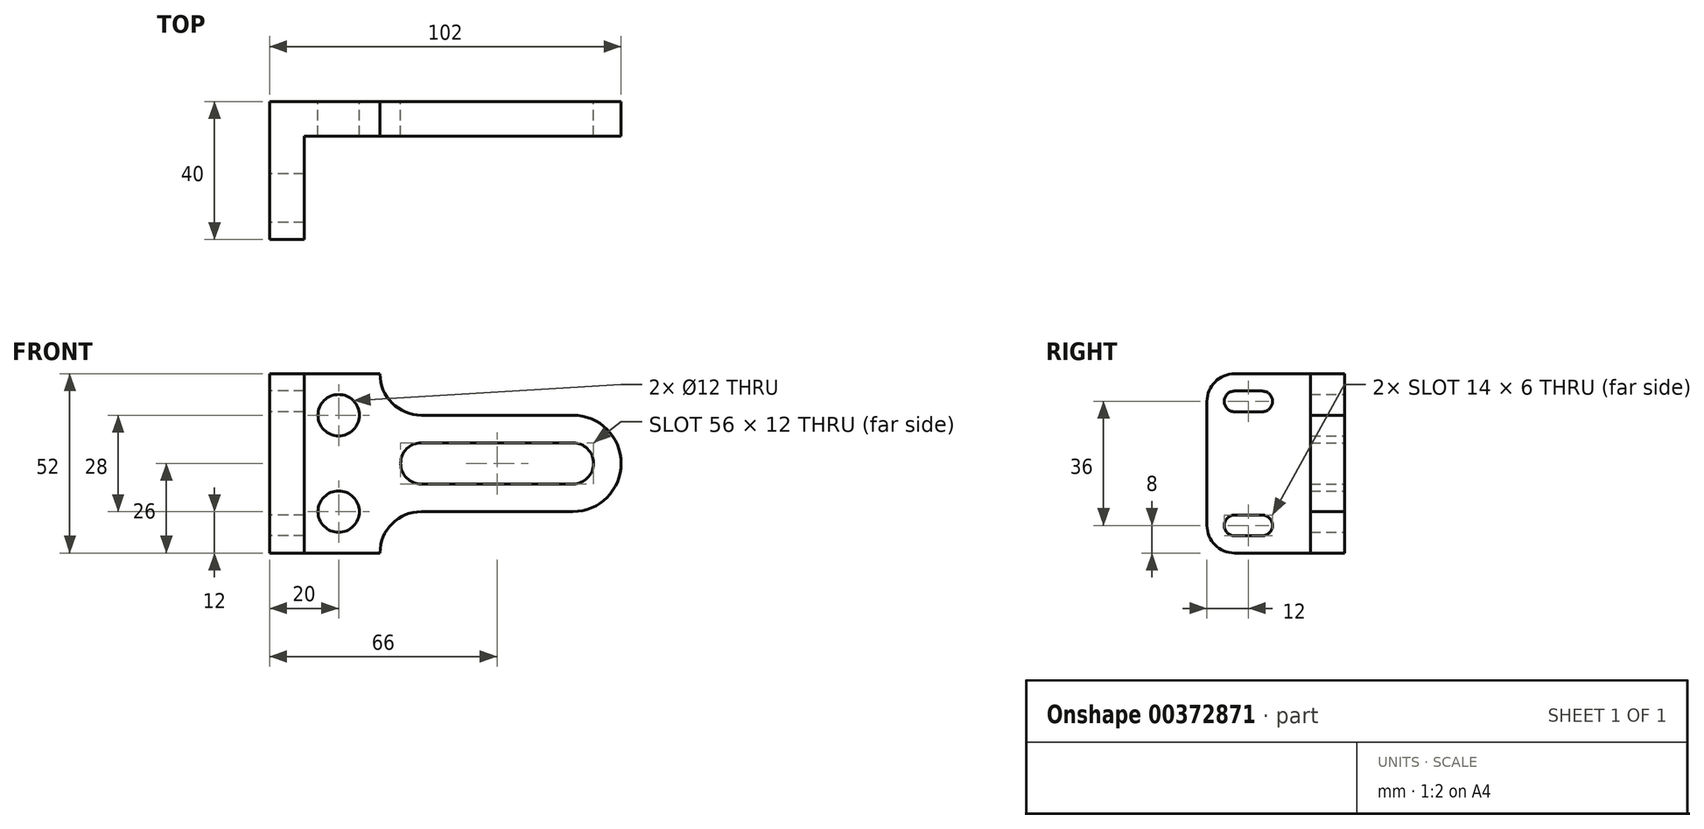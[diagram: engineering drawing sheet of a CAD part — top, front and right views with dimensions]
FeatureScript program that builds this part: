
annotation { "Feature Type Name" : "Feature", "Feature Type Description" : "" }
export const myFeature = defineFeature(function(context is Context, id is Id, definition is map)
    precondition{}
    {
        {
            var Q0;
            Q0=qCreatedBy(makeId("Front.planeOp"),FACE);
            var sketch = newSketch(context, id + "F0", { "sketchPlane" : qUnion([Q0])});
            skLineSegment(sketch, "E0", {"start": v(0, 52) * mm, "end": v(32, 52) * mm});
            skLineSegment(sketch, "E1", {"start": v(32, 52) * mm, "end": v(32, 40) * mm});
            skLineSegment(sketch, "E2", {"start": v(32, 40) * mm, "end": v(88, 40) * mm});
            skLineSegment(sketch, "E3", {"start": v(88, 12) * mm, "end": v(32, 12) * mm});
            skLineSegment(sketch, "E4", {"start": v(32, 12) * mm, "end": v(32, 0) * mm});
            skLineSegment(sketch, "E5", {"start": v(32, 0) * mm, "end": v(0, 0) * mm});
            skLineSegment(sketch, "E6", {"start": v(0, 0) * mm, "end": v(0, 52) * mm});
            skArc(sketch, "E7", {"start": v(88, 12) * mm, "mid": v(102, 26) * mm, "end": v(88, 40) * mm});
            skArc(sketch, "E8", {"start": v(44, 32) * mm, "mid": v(38, 26) * mm, "end": v(44, 20) * mm});
            skArc(sketch, "E9", {"start": v(88, 20) * mm, "mid": v(94, 26) * mm, "end": v(88, 32) * mm});
            skLineSegment(sketch, "E10", {"start": v(44, 32) * mm, "end": v(88, 32) * mm});
            skLineSegment(sketch, "E11", {"start": v(44, 20) * mm, "end": v(88, 20) * mm});
            skCircle(sketch, "E12", {"center": v(20, 40) * mm, "radius": 6 * mm});
            skCircle(sketch, "E13", {"center": v(20, 12) * mm, "radius": 6 * mm});
            skSolve(sketch);
        }
        {
            var Q0;
            Q0 = qSketchRegion(id + "F0", true);
            extrude(context, id + "F1", {"entities" : qUnion([Q0]), "depth" : 10 * mm});
        }
        {
            var Q0;
            Q0=qCreatedBy(makeId("Right.planeOp"),FACE);
            var sketch = newSketch(context, id + "F2", { "sketchPlane" : qUnion([Q0])});
            skLineSegment(sketch, "E14.bottom", {"start": v(0, 52) * mm, "end": v(-40, 52) * mm});
            skLineSegment(sketch, "E14.top", {"start": v(0, 0) * mm, "end": v(-40, 0) * mm});
            skLineSegment(sketch, "E14.left", {"start": v(0, 52) * mm, "end": v(0, 0) * mm});
            skLineSegment(sketch, "E14.right", {"start": v(-40, 52) * mm, "end": v(-40, 0) * mm});
            skSolve(sketch);
        }
        {
            var Q0;
            Q0 = qSketchRegion(id + "F2", true);
            extrude(context, id + "F3", {"entities" : qUnion([Q0]), "operationType" : NewBodyOperationType.ADD, "depth" : 10 * mm});
        }
        {
            var Q0;
            Q0=makeQuery(id+"F1.opExtrude","SWEPT_EDGE",EDGE,{"disambiguationData":[OSD([sQuery(id+"F0.wireOp",EDGE,"E1"),sQuery(id+"F0.wireOp",EDGE,"E2")])]});
            var Q1;
            Q1=makeQuery(id+"F1.opExtrude","SWEPT_EDGE",EDGE,{"disambiguationData":[OSD([sQuery(id+"F0.wireOp",EDGE,"E3"),sQuery(id+"F0.wireOp",EDGE,"E4")])]});
            fillet(context, id + "F4", {"entities" : qUnion([Q0, Q1]), "radius" : 12 * mm, "tangentPropagation" : true, "allowEdgeOverflow" : false});
        }
        {
            var Q0;
            Q0=makeQuery(id+"F3.opExtrude","SWEPT_EDGE",EDGE,{"disambiguationData":[OSD([sQuery(id+"F2.wireOp",EDGE,"E14.top"),sQuery(id+"F2.wireOp",EDGE,"E14.right")])]});
            var Q1;
            Q1=makeQuery(id+"F3.opExtrude","SWEPT_EDGE",EDGE,{"disambiguationData":[OSD([sQuery(id+"F2.wireOp",EDGE,"E14.bottom"),sQuery(id+"F2.wireOp",EDGE,"E14.right")])]});
            fillet(context, id + "F5", {"entities" : qUnion([Q0, Q1]), "radius" : 8 * mm, "tangentPropagation" : true, "allowEdgeOverflow" : false});
        }
        {
            var Q0;
            Q0=qCreatedBy(makeId("Right.planeOp"),FACE);
            var sketch = newSketch(context, id + "F6", { "sketchPlane" : qUnion([Q0])});
            skArc(sketch, "E15", {"start": v(-32, 11) * mm, "mid": v(-35, 8) * mm, "end": v(-32, 5) * mm});
            skArc(sketch, "E16", {"start": v(-24, 5) * mm, "mid": v(-21, 8) * mm, "end": v(-24, 11) * mm});
            skLineSegment(sketch, "E17", {"start": v(-32, 11) * mm, "end": v(-24, 11) * mm});
            skLineSegment(sketch, "E18", {"start": v(-32, 5) * mm, "end": v(-24, 5) * mm});
            skSolve(sketch);
        }
        {
            var Q0;
            Q0 = qSketchRegion(id + "F6", true);
            extrude(context, id + "F7", {"entities" : qUnion([Q0]), "operationType" : NewBodyOperationType.REMOVE, "endBound" : BoundingType.THROUGH_ALL, "depth" : 25 * mm});
        }
        {
            var Q0;
            Q0=makeQuery(id+"F3.boolean.opBoolean","MERGE",FACE,{"derivedFrom":[makeQuery(id+"F1.opExtrude","SWEPT_FACE",FACE,{"disambiguationData":[OSD([sQuery(id+"F0.wireOp",EDGE,"E0")])]}),makeQuery(id+"F3.opExtrude","SWEPT_FACE",FACE,{"disambiguationData":[OSD([sQuery(id+"F2.wireOp",EDGE,"E14.bottom")])]})]});
            var Q1;
            Q1=makeQuery(id+"F3.boolean.opBoolean","MERGE",FACE,{"derivedFrom":[makeQuery(id+"F1.opExtrude","SWEPT_FACE",FACE,{"disambiguationData":[OSD([sQuery(id+"F0.wireOp",EDGE,"E5")])]}),makeQuery(id+"F3.opExtrude","SWEPT_FACE",FACE,{"disambiguationData":[OSD([sQuery(id+"F2.wireOp",EDGE,"E14.top")])]})]});
            cPlane(context, id + "F8", {"entities" : qUnion([Q0, Q1]), "cplaneType" : CPlaneType.MID_PLANE, "offset" : 25 * mm, "width" : 150 * mm, "height" : 150 * mm});
        }
        {
            var Q0;
            Q0=makeQuery(id+"F1.opExtrude","SWEPT_BODY",BODY,{"disambiguationData":[OSD([sQuery(id+"F0.wireOp",EDGE,"E0"),sQuery(id+"F0.wireOp",EDGE,"E1"),sQuery(id+"F0.wireOp",EDGE,"E2"),sQuery(id+"F0.wireOp",EDGE,"E3"),sQuery(id+"F0.wireOp",EDGE,"E4"),sQuery(id+"F0.wireOp",EDGE,"E5"),sQuery(id+"F0.wireOp",EDGE,"E6"),sQuery(id+"F0.wireOp",EDGE,"E7"),sQuery(id+"F0.wireOp",EDGE,"E8"),sQuery(id+"F0.wireOp",EDGE,"E9"),sQuery(id+"F0.wireOp",EDGE,"E10"),sQuery(id+"F0.wireOp",EDGE,"E11"),sQuery(id+"F0.wireOp",EDGE,"E12"),sQuery(id+"F0.wireOp",EDGE,"E13")])]});
            var Q1;
            Q1=qCreatedBy(id+"F8.planeOp",FACE);
            mirror(context, id + "F9", {"operationType" : NewBodyOperationType.INTERSECT, "entities" : qUnion([Q0]), "mirrorPlane" : qUnion([Q1])});
        }
    });
